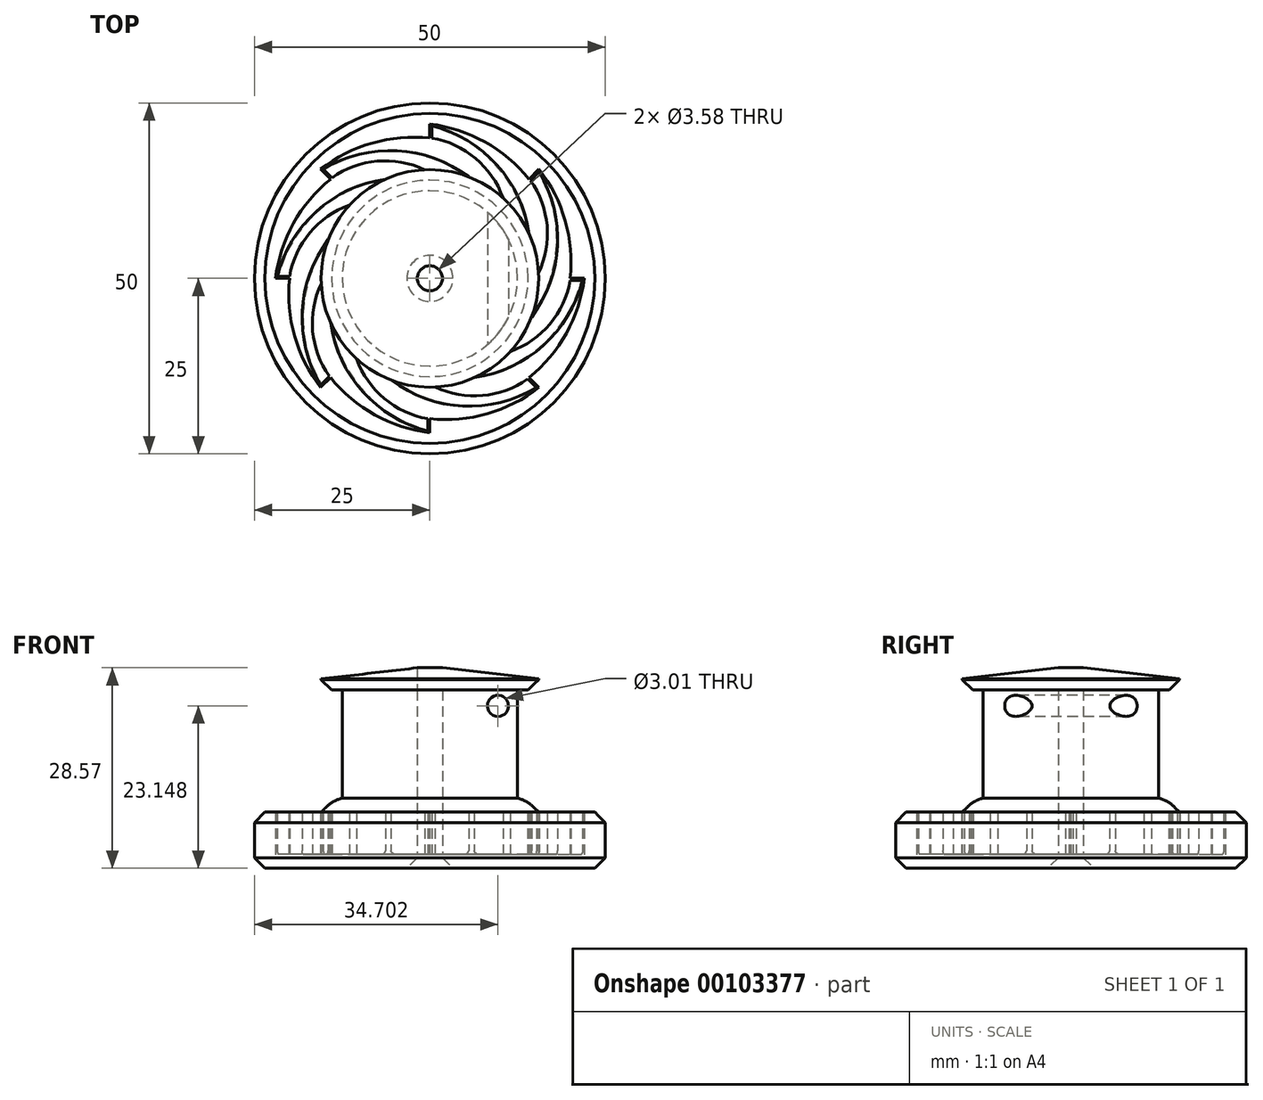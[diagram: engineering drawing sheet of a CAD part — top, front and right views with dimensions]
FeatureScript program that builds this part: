
annotation { "Feature Type Name" : "Feature", "Feature Type Description" : "" }
export const myFeature = defineFeature(function(context is Context, id is Id, definition is map)
    precondition{}
    {
        {
            var Q0;
            Q0=qCreatedBy(makeId("Top.planeOp"),FACE);
            var sketch = newSketch(context, id + "F0", { "sketchPlane" : qUnion([Q0])});
            skCircle(sketch, "E0", {"center": v(0, 0) * mm, "radius": 25 * mm});
            skCircle(sketch, "E1", {"center": v(0, 0) * mm, "radius": 1.8 * mm});
            skArc(sketch, "E2", {"start": v(-0.75, 15.48) * mm, "mid": v(-3.6, 15.08) * mm, "end": v(-6.33, 14.15) * mm});
            skLineSegment(sketch, "E3", {"start": v(0, 25) * mm, "end": v(0, -25) * mm, "construction": true});
            skLineSegment(sketch, "E4", {"start": v(-25, 0) * mm, "end": v(25, 0) * mm, "construction": true});
            skLineSegment(sketch, "E5", {"start": v(-17.68, 17.68) * mm, "end": v(17.68, -17.68) * mm, "construction": true});
            skLineSegment(sketch, "E6", {"start": v(17.68, 17.68) * mm, "end": v(-17.68, -17.68) * mm, "construction": true});
            skArc(sketch, "E7", {"start": v(0, 20) * mm, "mid": v(-8.2, 19.29) * mm, "end": v(-15.56, 15.56) * mm});
            skLineSegment(sketch, "E8", {"start": v(0, 22) * mm, "end": v(0, 20) * mm});
            skLineSegment(sketch, "E9", {"start": v(0.28, 20) * mm, "end": v(0.28, 21.75) * mm});
            skArc(sketch, "E10.1.0", {"start": v(-14.14, 14.14) * mm, "mid": v(-19.44, 7.83) * mm, "end": v(-22, 0) * mm});
            skLineSegment(sketch, "E10.1.1", {"start": v(-15.56, 15.56) * mm, "end": v(-14.14, 14.14) * mm});
            skArc(sketch, "E10.2.0", {"start": v(-20, 0) * mm, "mid": v(-19.29, -8.2) * mm, "end": v(-15.56, -15.56) * mm});
            skLineSegment(sketch, "E10.2.1", {"start": v(-22, 0) * mm, "end": v(-20, 0) * mm});
            skArc(sketch, "E10.3.0", {"start": v(-14.14, -14.14) * mm, "mid": v(-7.83, -19.44) * mm, "end": v(0, -22) * mm});
            skLineSegment(sketch, "E10.3.1", {"start": v(-15.56, -15.56) * mm, "end": v(-14.14, -14.14) * mm});
            skArc(sketch, "E10.4.0", {"start": v(0, -20) * mm, "mid": v(8.2, -19.29) * mm, "end": v(15.56, -15.56) * mm});
            skLineSegment(sketch, "E10.4.1", {"start": v(0, -22) * mm, "end": v(0, -20) * mm});
            skArc(sketch, "E10.5.0", {"start": v(14.14, -14.14) * mm, "mid": v(19.44, -7.83) * mm, "end": v(22, 0) * mm});
            skLineSegment(sketch, "E10.5.1", {"start": v(15.56, -15.56) * mm, "end": v(14.14, -14.14) * mm});
            skArc(sketch, "E10.6.0", {"start": v(20, 0) * mm, "mid": v(19.29, 8.2) * mm, "end": v(15.56, 15.56) * mm});
            skLineSegment(sketch, "E10.6.1", {"start": v(22, 0) * mm, "end": v(20, 0) * mm});
            skArc(sketch, "E10.7.0", {"start": v(14.14, 14.14) * mm, "mid": v(7.83, 19.44) * mm, "end": v(0, 22) * mm});
            skLineSegment(sketch, "E10.7.1", {"start": v(15.56, 15.56) * mm, "end": v(14.14, 14.14) * mm});
            skArc(sketch, "E11", {"start": v(14.15, 6.33) * mm, "mid": v(9.57, 16.16) * mm, "end": v(0.28, 21.75) * mm});
            skArc(sketch, "E12", {"start": v(10.42, 11.48) * mm, "mid": v(6.5, 17.12) * mm, "end": v(0.28, 20) * mm});
            skArc(sketch, "E13.1.0", {"start": v(-0.75, 15.48) * mm, "mid": v(-7.5, 16.7) * mm, "end": v(-13.94, 14.34) * mm});
            skArc(sketch, "E13.1.1", {"start": v(5.53, 14.48) * mm, "mid": v(-4.66, 18.2) * mm, "end": v(-15.18, 15.57) * mm});
            skLineSegment(sketch, "E13.1.2", {"start": v(-13.94, 14.34) * mm, "end": v(-15.18, 15.57) * mm});
            skArc(sketch, "E13.2.0", {"start": v(-11.48, 10.42) * mm, "mid": v(-17.12, 6.5) * mm, "end": v(-20, 0.28) * mm});
            skArc(sketch, "E13.2.1", {"start": v(-6.33, 14.15) * mm, "mid": v(-16.16, 9.57) * mm, "end": v(-21.75, 0.28) * mm});
            skLineSegment(sketch, "E13.2.2", {"start": v(-20, 0.28) * mm, "end": v(-21.75, 0.28) * mm});
            skArc(sketch, "E13.3.0", {"start": v(-15.48, -0.75) * mm, "mid": v(-16.7, -7.5) * mm, "end": v(-14.34, -13.94) * mm});
            skArc(sketch, "E13.3.1", {"start": v(-14.48, 5.53) * mm, "mid": v(-18.2, -4.66) * mm, "end": v(-15.57, -15.18) * mm});
            skLineSegment(sketch, "E13.3.2", {"start": v(-14.34, -13.94) * mm, "end": v(-15.57, -15.18) * mm});
            skArc(sketch, "E13.4.0", {"start": v(-10.42, -11.48) * mm, "mid": v(-6.5, -17.12) * mm, "end": v(-0.28, -20) * mm});
            skArc(sketch, "E13.4.1", {"start": v(-14.15, -6.33) * mm, "mid": v(-9.57, -16.16) * mm, "end": v(-0.28, -21.75) * mm});
            skLineSegment(sketch, "E13.4.2", {"start": v(-0.28, -20) * mm, "end": v(-0.28, -21.75) * mm});
            skArc(sketch, "E13.5.0", {"start": v(0.75, -15.48) * mm, "mid": v(7.5, -16.7) * mm, "end": v(13.94, -14.34) * mm});
            skArc(sketch, "E13.5.1", {"start": v(-5.53, -14.48) * mm, "mid": v(4.66, -18.2) * mm, "end": v(15.18, -15.57) * mm});
            skLineSegment(sketch, "E13.5.2", {"start": v(13.94, -14.34) * mm, "end": v(15.18, -15.57) * mm});
            skArc(sketch, "E13.6.0", {"start": v(11.48, -10.42) * mm, "mid": v(17.12, -6.5) * mm, "end": v(20, -0.28) * mm});
            skArc(sketch, "E13.6.1", {"start": v(6.33, -14.15) * mm, "mid": v(16.16, -9.57) * mm, "end": v(21.75, -0.28) * mm});
            skLineSegment(sketch, "E13.6.2", {"start": v(20, -0.28) * mm, "end": v(21.75, -0.28) * mm});
            skArc(sketch, "E13.7.0", {"start": v(15.48, 0.75) * mm, "mid": v(16.7, 7.5) * mm, "end": v(14.34, 13.94) * mm});
            skArc(sketch, "E13.7.1", {"start": v(14.48, -5.53) * mm, "mid": v(18.2, 4.66) * mm, "end": v(15.57, 15.18) * mm});
            skLineSegment(sketch, "E13.7.2", {"start": v(14.34, 13.94) * mm, "end": v(15.57, 15.18) * mm});
            skArc(sketch, "E14.trimOffspring", {"start": v(10.42, 11.48) * mm, "mid": v(8.11, 13.2) * mm, "end": v(5.53, 14.48) * mm});
            skArc(sketch, "E15.trimOffspring", {"start": v(15.48, 0.75) * mm, "mid": v(15.08, 3.6) * mm, "end": v(14.15, 6.33) * mm});
            skArc(sketch, "E16.trimOffspring", {"start": v(11.48, -10.42) * mm, "mid": v(13.2, -8.11) * mm, "end": v(14.48, -5.53) * mm});
            skArc(sketch, "E17.trimOffspring", {"start": v(-11.48, 10.42) * mm, "mid": v(-13.2, 8.11) * mm, "end": v(-14.48, 5.53) * mm});
            skArc(sketch, "E18.trimOffspring", {"start": v(-15.48, -0.75) * mm, "mid": v(-15.08, -3.6) * mm, "end": v(-14.15, -6.33) * mm});
            skArc(sketch, "E19.trimOffspring", {"start": v(-10.42, -11.48) * mm, "mid": v(-8.11, -13.2) * mm, "end": v(-5.53, -14.48) * mm});
            skArc(sketch, "E20.trimOffspring", {"start": v(0.75, -15.48) * mm, "mid": v(3.6, -15.08) * mm, "end": v(6.33, -14.15) * mm});
            skSolve(sketch);
        }
        {
            var Q0;
            Q0=makeQuery(id+"F0.imprint","IMPRINT",FACE,{"disambiguationData":[TD([[makeQuery(id+"F0.imprint","IMPRINT",EDGE,{"derivedFrom":sQuery(id+"F0.wireOp",EDGE,"E0")}),1.0]])]});
            var Q1;
            Q1=makeQuery(id+"F0.imprint","IMPRINT",FACE,{"disambiguationData":[TD([[makeQuery(id+"F0.imprint","IMPRINT",EDGE,{"derivedFrom":sQuery(id+"F0.wireOp",EDGE,"E2")}),-1.0]])]});
            var Q2;
            Q2=makeQuery(id+"F0.imprint","IMPRINT",FACE,{"disambiguationData":[TD([[makeQuery(id+"F0.imprint","IMPRINT",EDGE,{"derivedFrom":sQuery(id+"F0.wireOp",EDGE,"E1")}),-1.0]])]});
            extrude(context, id + "F1", {"entities" : qUnion([Q0, Q1, Q2]), "oppositeDirection" : true, "depth" : 1.5 * mm});
        }
        {
            var Q0;
            Q0=makeQuery(id+"F0.imprint","IMPRINT",FACE,{"disambiguationData":[TD([[makeQuery(id+"F0.imprint","IMPRINT",EDGE,{"derivedFrom":sQuery(id+"F0.wireOp",EDGE,"E0")}),1.0]])]});
            extrude(context, id + "F2", {"entities" : qUnion([Q0]), "operationType" : NewBodyOperationType.ADD, "depth" : 6.5 * mm});
        }
        {
            var Q0;
            Q0=makeQuery(id+"F0.imprint","IMPRINT",FACE,{"disambiguationData":[TD([[makeQuery(id+"F0.imprint","IMPRINT",EDGE,{"derivedFrom":sQuery(id+"F0.wireOp",EDGE,"E1")}),-1.0]])]});
            var sketch = newSketch(context, id + "F3", { "sketchPlane" : qUnion([Q0])});
            skCircle(sketch, "E21.0", {"center": v(0, 0) * mm, "radius": 1.8 * mm});
            skCircle(sketch, "E22", {"center": v(0, 0) * mm, "radius": 5 * mm});
            skSolve(sketch);
        }
        {
            var Q0;
            Q0=qCreatedBy(makeId("Right.planeOp"),FACE);
            var sketch = newSketch(context, id + "F4", { "sketchPlane" : qUnion([Q0])});
            skLineSegment(sketch, "E23", {"start": v(0, 0) * mm, "end": v(0, 0.5) * mm, "construction": true});
            skLineSegment(sketch, "E24.0", {"start": v(-5, 0) * mm, "end": v(5, 0) * mm});
            skLineSegment(sketch, "E25.0", {"start": v(-1.8, 0) * mm, "end": v(1.8, 0) * mm});
            skLineSegment(sketch, "E26", {"start": v(-1.8, 0) * mm, "end": v(-1.8, 0.5) * mm});
            skLineSegment(sketch, "E27", {"start": v(-5, 0) * mm, "end": v(-1.8, 0.5) * mm});
            skSolve(sketch);
        }
        {
            var Q0;
            {var subQ2=sQuery(id+"F4.wireOp",EDGE,"E26");Q0=makeQuery(id+"F4.imprint","IMPRINT",FACE,{"disambiguationData":[TD([[makeQuery(id+"F4.imprint","IMPRINT",EDGE,{"derivedFrom":subQ2}),1.0]])]});}
            var Q1;
            Q1=sQuery(id+"F4.wireOp",EDGE,"E23");
            revolve(context, id + "F5", {"operationType" : NewBodyOperationType.ADD, "entities" : qUnion([Q0]), "axis" : qUnion([Q1]), "revolveType" : RevolveType.FULL});
        }
        {
            var Q0;
            Q0=makeQuery(id+"F0.imprint","IMPRINT",FACE,{"disambiguationData":[TD([[makeQuery(id+"F0.imprint","IMPRINT",EDGE,{"derivedFrom":sQuery(id+"F0.wireOp",EDGE,"E1")}),-1.0]])]});
            extrude(context, id + "F6", {"entities" : qUnion([Q0]), "depth" : 6.5 * mm});
        }
        {
            var Q0;
            Q0=makeQuery(id+"F6.opExtrude","CAP_FACE",FACE,{"disambiguationData":[OSD([sQuery(id+"F0.wireOp",EDGE,"E1"),sQuery(id+"F0.wireOp",EDGE,"E2"),sQuery(id+"F0.wireOp",EDGE,"E9"),sQuery(id+"F0.wireOp",EDGE,"E11"),sQuery(id+"F0.wireOp",EDGE,"E12"),sQuery(id+"F0.wireOp",EDGE,"E13.1.0"),sQuery(id+"F0.wireOp",EDGE,"E13.1.1"),sQuery(id+"F0.wireOp",EDGE,"E13.1.2"),sQuery(id+"F0.wireOp",EDGE,"E13.2.0"),sQuery(id+"F0.wireOp",EDGE,"E13.2.1"),sQuery(id+"F0.wireOp",EDGE,"E13.2.2"),sQuery(id+"F0.wireOp",EDGE,"E13.3.0"),sQuery(id+"F0.wireOp",EDGE,"E13.3.1"),sQuery(id+"F0.wireOp",EDGE,"E13.3.2"),sQuery(id+"F0.wireOp",EDGE,"E13.4.0"),sQuery(id+"F0.wireOp",EDGE,"E13.4.1"),sQuery(id+"F0.wireOp",EDGE,"E13.4.2"),sQuery(id+"F0.wireOp",EDGE,"E13.5.0"),sQuery(id+"F0.wireOp",EDGE,"E13.5.1"),sQuery(id+"F0.wireOp",EDGE,"E13.5.2"),sQuery(id+"F0.wireOp",EDGE,"E13.6.0"),sQuery(id+"F0.wireOp",EDGE,"E13.6.1"),sQuery(id+"F0.wireOp",EDGE,"E13.6.2"),sQuery(id+"F0.wireOp",EDGE,"E13.7.0"),sQuery(id+"F0.wireOp",EDGE,"E13.7.1"),sQuery(id+"F0.wireOp",EDGE,"E13.7.2"),sQuery(id+"F0.wireOp",EDGE,"E14.trimOffspring"),sQuery(id+"F0.wireOp",EDGE,"E15.trimOffspring"),sQuery(id+"F0.wireOp",EDGE,"E16.trimOffspring"),sQuery(id+"F0.wireOp",EDGE,"E17.trimOffspring"),sQuery(id+"F0.wireOp",EDGE,"E18.trimOffspring"),sQuery(id+"F0.wireOp",EDGE,"E19.trimOffspring"),sQuery(id+"F0.wireOp",EDGE,"E20.trimOffspring")])],"isStart":false});
            var sketch = newSketch(context, id + "F7", { "sketchPlane" : qUnion([Q0])});
            skCircle(sketch, "E28.0", {"center": v(0, 0) * mm, "radius": 1.8 * mm});
            skCircle(sketch, "E29", {"center": v(0, 0) * mm, "radius": 15.5 * mm});
            skCircle(sketch, "E30", {"center": v(0, 0) * mm, "radius": 12.5 * mm});
            skSolve(sketch);
        }
        {
            var Q0;
            Q0=makeQuery(id+"F7.imprint","IMPRINT",FACE,{"disambiguationData":[TD([[makeQuery(id+"F7.imprint","IMPRINT",EDGE,{"derivedFrom":sQuery(id+"F7.wireOp",EDGE,"E28.0")}),-1.0]])]});
            extrude(context, id + "F8", {"entities" : qUnion([Q0]), "operationType" : NewBodyOperationType.ADD, "depth" : 17.4 * mm});
        }
        {
            var Q0;
            Q0=makeQuery(id+"F7.imprint","IMPRINT",FACE,{"disambiguationData":[TD([[makeQuery(id+"F7.imprint","IMPRINT",EDGE,{"derivedFrom":sQuery(id+"F7.wireOp",EDGE,"E30")}),-1.0]])]});
            extrude(context, id + "F9", {"entities" : qUnion([Q0]), "operationType" : NewBodyOperationType.ADD, "depth" : 2 * mm});
        }
        {
            var Q0;
            Q0=makeQuery(id+"F9.opExtrude","CAP_EDGE",EDGE,{"disambiguationData":[OSD([sQuery(id+"F7.wireOp",EDGE,"E29")])],"isStart":false});
            chamfer(context, id + "F10", {"entities" : qUnion([Q0]), "width" : 2 * mm, "tangentPropagation" : true});
        }
        {
            var Q0;
            {var subQ0=sQuery(id+"F7.wireOp",EDGE,"E29");Q0=makeQuery(id+"F10.opChamfer","BLEND_EDGE",EDGE,{"blendedFrom":[makeQuery(id+"F9.opExtrude","CAP_EDGE",EDGE,{"disambiguationData":[OSD([subQ0])],"isStart":false}),makeQuery(id+"F9.opExtrude","CAP_FACE",FACE,{"disambiguationData":[OSD([subQ0,sQuery(id+"F7.wireOp",EDGE,"E30")])],"isStart":false})],"blendedInto":[makeQuery(id+"F9.opExtrude","CAP_FACE",FACE,{"disambiguationData":[OSD([subQ0,sQuery(id+"F7.wireOp",EDGE,"E30")])],"isStart":false})]});}
            fillet(context, id + "F11", {"entities" : qUnion([Q0]), "radius" : 5 * mm, "tangentPropagation" : true, "allowEdgeOverflow" : false});
        }
        {
            var Q0;
            Q0=makeQuery(id+"F8.opExtrude","CAP_FACE",FACE,{"disambiguationData":[OSD([sQuery(id+"F7.wireOp",EDGE,"E28.0"),sQuery(id+"F7.wireOp",EDGE,"E30")])],"isStart":false});
            var sketch = newSketch(context, id + "F12", { "sketchPlane" : qUnion([Q0])});
            skCircle(sketch, "E31.0", {"center": v(0, 0) * mm, "radius": 15.5 * mm});
            skCircle(sketch, "E32.0", {"center": v(0, 0) * mm, "radius": 1.8 * mm});
            skSolve(sketch);
        }
        {
            var Q0;
            Q0=makeQuery(id+"F12.imprint","IMPRINT",FACE,{"disambiguationData":[TD([[makeQuery(id+"F12.imprint","IMPRINT",EDGE,{"derivedFrom":sQuery(id+"F12.wireOp",EDGE,"E31.0")}),1.0]])]});
            var Q1;
            Q1=makeQuery(id+"F12.imprint","IMPRINT",FACE,{"disambiguationData":[TD([[makeQuery(id+"F12.imprint","IMPRINT",EDGE,{"derivedFrom":sQuery(id+"F12.wireOp",EDGE,"E32.0")}),-1.0]])]});
            extrude(context, id + "F13", {"entities" : qUnion([Q0, Q1]), "depth" : 1.59 * mm});
        }
        {
            var Q0;
            Q0=qCreatedBy(makeId("Front.planeOp"),FACE);
            var sketch = newSketch(context, id + "F14", { "sketchPlane" : qUnion([Q0])});
            skLineSegment(sketch, "E33.0", {"start": v(-1.8, 25.49) * mm, "end": v(1.8, 25.49) * mm});
            skLineSegment(sketch, "E34", {"start": v(1.8, 25.49) * mm, "end": v(1.8, 27.07) * mm});
            skLineSegment(sketch, "E35.0", {"start": v(-15.5, 25.49) * mm, "end": v(15.5, 25.49) * mm});
            skLineSegment(sketch, "E36", {"start": v(15.5, 25.49) * mm, "end": v(1.8, 27.07) * mm});
            skLineSegment(sketch, "E37", {"start": v(0, 25.49) * mm, "end": v(0, 28.38) * mm, "construction": true});
            skPoint(sketch, "E37.endSnap0", {"position": v(0, 25.49) * mm});
            skSolve(sketch);
        }
        {
            var Q0;
            {var subQ0=sQuery(id+"F14.wireOp",EDGE,"E34");Q0=makeQuery(id+"F14.imprint","IMPRINT",FACE,{"disambiguationData":[TD([[makeQuery(id+"F14.imprint","IMPRINT",EDGE,{"derivedFrom":subQ0}),-1.0]])]});}
            var Q1;
            Q1=sQuery(id+"F14.wireOp",EDGE,"E37");
            revolve(context, id + "F15", {"operationType" : NewBodyOperationType.ADD, "entities" : qUnion([Q0]), "axis" : qUnion([Q1]), "revolveType" : RevolveType.FULL});
        }
        {
            var Q0;
            Q0=makeQuery(id+"F13.opExtrude","CAP_EDGE",EDGE,{"disambiguationData":[OSD([sQuery(id+"F12.wireOp",EDGE,"E31.0")])],"isStart":true});
            var Q1;
            Q1=makeQuery(id+"F2.opExtrude","CAP_EDGE",EDGE,{"disambiguationData":[OSD([sQuery(id+"F0.wireOp",EDGE,"E0")])],"isStart":false});
            var Q2;
            Q2=makeQuery(id+"F1.opExtrude","CAP_FACE",FACE,{"disambiguationData":[OSD([sQuery(id+"F0.wireOp",EDGE,"E0"),sQuery(id+"F0.wireOp",EDGE,"E1")])],"isStart":false});
            chamfer(context, id + "F16", {"entities" : qUnion([Q0, Q1, Q2]), "width" : 1.5 * mm, "tangentPropagation" : true});
        }
        {
            var Q0;
            Q0=makeQuery(id+"F1.opExtrude","CAP_EDGE",EDGE,{"disambiguationData":[OSD([sQuery(id+"F0.wireOp",EDGE,"E0")])],"isStart":false});
            var Q1;
            Q1=makeQuery(id+"F2.opExtrude","CAP_EDGE",EDGE,{"disambiguationData":[OSD([sQuery(id+"F0.wireOp",EDGE,"E0")])],"isStart":false});
            var Q2;
            Q2=makeQuery(id+"F6.opExtrude","CAP_EDGE",EDGE,{"disambiguationData":[OSD([sQuery(id+"F0.wireOp",EDGE,"E13.4.1")])],"isStart":true});
            var Q3;
            Q3=makeQuery(id+"F6.opExtrude","CAP_EDGE",EDGE,{"disambiguationData":[OSD([sQuery(id+"F0.wireOp",EDGE,"E13.3.1")])],"isStart":true});
            var Q4;
            Q4=makeQuery(id+"F6.opExtrude","CAP_EDGE",EDGE,{"disambiguationData":[OSD([sQuery(id+"F0.wireOp",EDGE,"E13.2.1")])],"isStart":true});
            var Q5;
            Q5=makeQuery(id+"F6.opExtrude","CAP_EDGE",EDGE,{"disambiguationData":[OSD([sQuery(id+"F0.wireOp",EDGE,"E13.1.1")])],"isStart":true});
            var Q6;
            Q6=makeQuery(id+"F6.opExtrude","CAP_EDGE",EDGE,{"disambiguationData":[OSD([sQuery(id+"F0.wireOp",EDGE,"E11")])],"isStart":true});
            var Q7;
            Q7=makeQuery(id+"F6.opExtrude","CAP_EDGE",EDGE,{"disambiguationData":[OSD([sQuery(id+"F0.wireOp",EDGE,"E13.7.1")])],"isStart":true});
            var Q8;
            Q8=makeQuery(id+"F6.opExtrude","CAP_EDGE",EDGE,{"disambiguationData":[OSD([sQuery(id+"F0.wireOp",EDGE,"E13.6.1")])],"isStart":true});
            var Q9;
            Q9=makeQuery(id+"F6.opExtrude","CAP_EDGE",EDGE,{"disambiguationData":[OSD([sQuery(id+"F0.wireOp",EDGE,"E13.5.1")])],"isStart":true});
            fillet(context, id + "F17", {"entities" : qUnion([Q0, Q1, Q2, Q3, Q4, Q5, Q6, Q7, Q8, Q9]), "radius" : 1 * mm, "tangentPropagation" : true, "allowEdgeOverflow" : false});
        }
        {
            var Q0;
            Q0=makeQuery(id+"F0.imprint","IMPRINT",FACE,{"disambiguationData":[TD([[makeQuery(id+"F0.imprint","IMPRINT",EDGE,{"derivedFrom":sQuery(id+"F0.wireOp",EDGE,"E1")}),-1.0]])]});
            extrude(context, id + "F18", {"entities" : qUnion([Q0]), "operationType" : NewBodyOperationType.REMOVE, "depth" : .5 * mm});
        }
        {
            var Q0;
            Q0=qCreatedBy(makeId("Front.planeOp"),FACE);
            var sketch = newSketch(context, id + "F19", { "sketchPlane" : qUnion([Q0])});
            skLineSegment(sketch, "E38", {"start": v(0, 0) * mm, "end": v(0, 21.65) * mm, "construction": true});
            skLineSegment(sketch, "E39", {"start": v(0, 21.65) * mm, "end": v(9.7, 21.65) * mm, "construction": true});
            skCircle(sketch, "E40", {"center": v(9.7, 21.65) * mm, "radius": 1.5 * mm});
            skSolve(sketch);
        }
        {
            var Q0;
            Q0 = qSketchRegion(id + "F19", true);
            extrude(context, id + "F20", {"entities" : qUnion([Q0]), "operationType" : NewBodyOperationType.REMOVE, "endBound" : BoundingType.SYMMETRIC, "oppositeDirection" : true, "depth" : 25 * mm});
        }
    });
